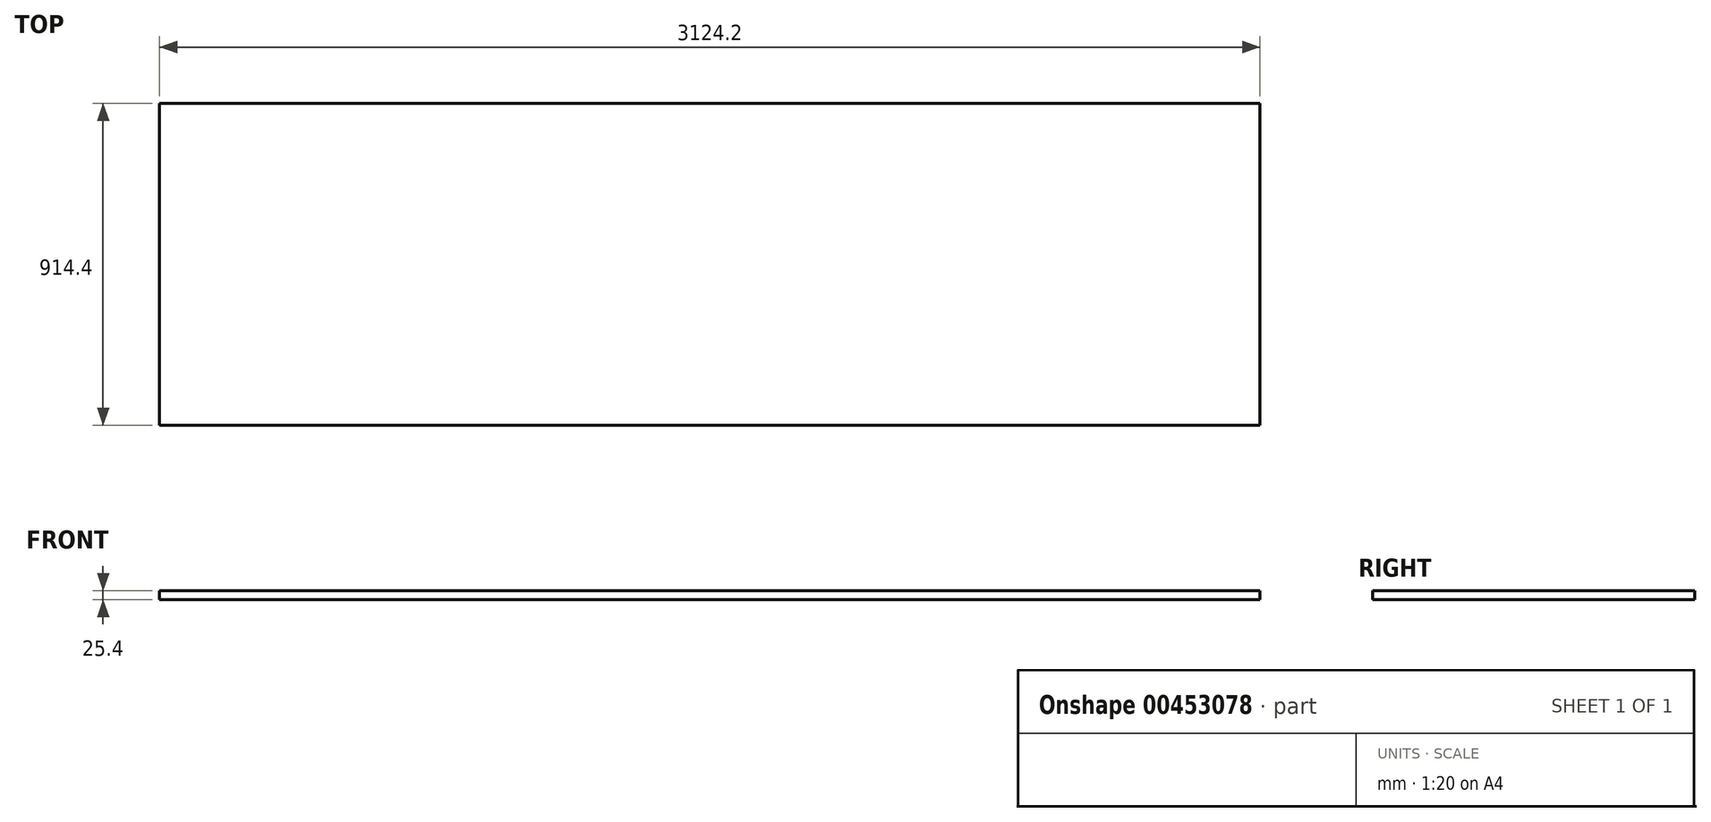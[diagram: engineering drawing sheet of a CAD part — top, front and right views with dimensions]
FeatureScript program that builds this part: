
annotation { "Feature Type Name" : "Feature", "Feature Type Description" : "" }
export const myFeature = defineFeature(function(context is Context, id is Id, definition is map)
    precondition{}
    {
        {
            var Q0;
            Q0=qCreatedBy(makeId("Top.planeOp"),FACE);
            var sketch = newSketch(context, id + "F0", { "sketchPlane" : qUnion([Q0])});
            skLineSegment(sketch, "E0.bottom", {"start": v(1562.1, 457.2) * mm, "end": v(-1562.1, 457.2) * mm});
            skLineSegment(sketch, "E0.top", {"start": v(1562.1, -457.2) * mm, "end": v(-1562.1, -457.2) * mm});
            skLineSegment(sketch, "E0.left", {"start": v(1562.1, 457.2) * mm, "end": v(1562.1, -457.2) * mm});
            skLineSegment(sketch, "E0.right", {"start": v(-1562.1, 457.2) * mm, "end": v(-1562.1, -457.2) * mm});
            skPoint(sketch, "E0.middle", {"position": v(0, 0) * mm});
            skSolve(sketch);
        }
        {
            var Q0;
            Q0 = qSketchRegion(id + "F0", true);
            extrude(context, id + "F1", {"entities" : qUnion([Q0]), "depth" : 25.4 * mm, "offsetDistance" : 25.4 * mm});
        }
    });
